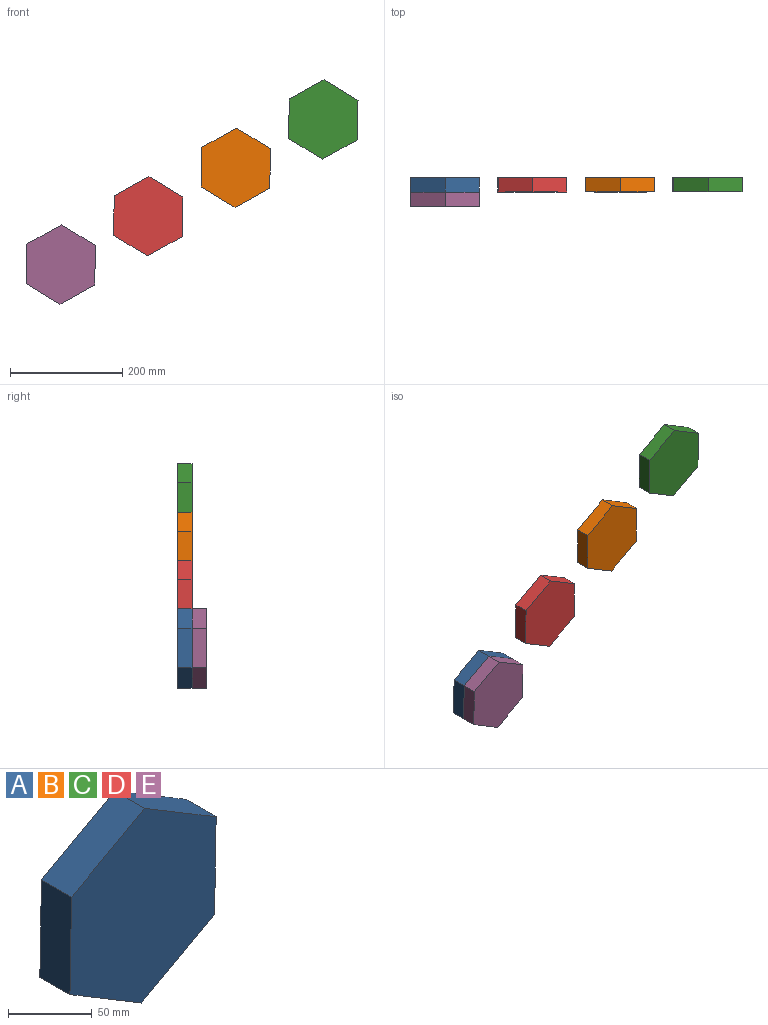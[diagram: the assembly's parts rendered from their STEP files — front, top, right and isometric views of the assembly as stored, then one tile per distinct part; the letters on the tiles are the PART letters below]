
ASSEMBLY  parts=5 mates=1
PART A: 8 faces, bbox 123.5x25.4x141.1 mm
  f0: plane 70.53x25.4mm, normal (1,0,-0.02), area 1791.7mm2, adj f1,f5,f6,f7
  f1: plane 60.42x36.41mm, normal (0.52,0,0.86), area 1791.7mm2, adj f0,f2,f6,f7
  f2: plane 61.74x34.12mm, normal (-0.48,0,0.88), area 1791.7mm2, adj f1,f3,f6,f7
  f3: plane 70.53x25.4mm, normal (-1,0,0.02), area 1791.7mm2, adj f2,f4,f6,f7
  f4: plane 60.42x36.41mm, normal (-0.52,0,-0.86), area 1791.7mm2, adj f3,f5,f6,f7
  f5: plane 61.74x34.12mm, normal (0.48,0,-0.88), area 1791.7mm2, adj f0,f4,f6,f7
  f6: plane 141.05x123.47mm, normal (0,-1,0), area 12927.1mm2, adj f0,f1,f2,f3,f4,f5
  f7: plane 141.05x123.47mm, normal (0,1,0), area 12927.1mm2, adj f0,f1,f2,f3,f4,f5
PART B: same geometry as A
PART C: same geometry as A
PART D: same geometry as A
PART E: same geometry as A
PLACE A t=(518.66,-172.06,-115.49)mm
PLACE B t=(829.89,-172.06,56.52)mm
PLACE C t=(985.5,-172.06,142.52)mm
PLACE D t=(674.27,-172.06,-29.49)mm
PLACE E t=(518.66,-197.46,-115.49)mm
MATE fastened A.f6 <-> E.f7  axis (0,-1,0) through (518.66,-197.46,-115.49)mm
